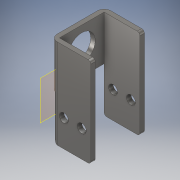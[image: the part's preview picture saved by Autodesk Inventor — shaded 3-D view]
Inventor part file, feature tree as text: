
AUTODESK INVENTOR PART (.ipt)
format: ipt  version: 2017 (Build 210142000, 142)  size: 173,568 bytes
history: native  units: in
note: dims shown in document units (in); Inventor stores cm internally (conversion verified against a paired STEP export)
features: fillet x6, sketch x3, extrude x3, plane x1
ambient origin geometry x8: Origin, YZ Plane, XZ Plane, XY Plane, X Axis, Y Axis, Z Axis, Center Point
bodies: Solid1 (feature_tree)
feature tree (13):
  sketch  "Sketch1"  dims[d0=1.0in d1=1.0in]
  plane  "Work Plane2"
  extrude  "Extrusion2"  Depth=1.0in
  extrude  "Extrusion3"  Depth=0.1in
  extrude  "Extrusion4"  Depth=0.15in
  fillet  "Fillet1"  Radius=1.0in
  fillet  "Fillet2"  Radius=0.8in
  fillet  "Fillet3"  Radius=0.1in
  fillet  "Fillet4"  Radius=1.5875in
  fillet  "Fillet5"  Radius=0.0625in
  fillet  "Fillet6"  Radius=0.0625in
  sketch  "Sketch2"  dims[d2=0.1in d3=0.1in]
  sketch  "Sketch3"  dims[d10=0.1in d11=1.0in d12=1.0in d13=0.8in d14=0.0in d18=0.1in d19=0.0in d25=1.5875in d26=0.0in d27=0.0625in d28=0.0625in d29=0.0625in d30=0.0625in d31=0.0625in d32=0.15in]
